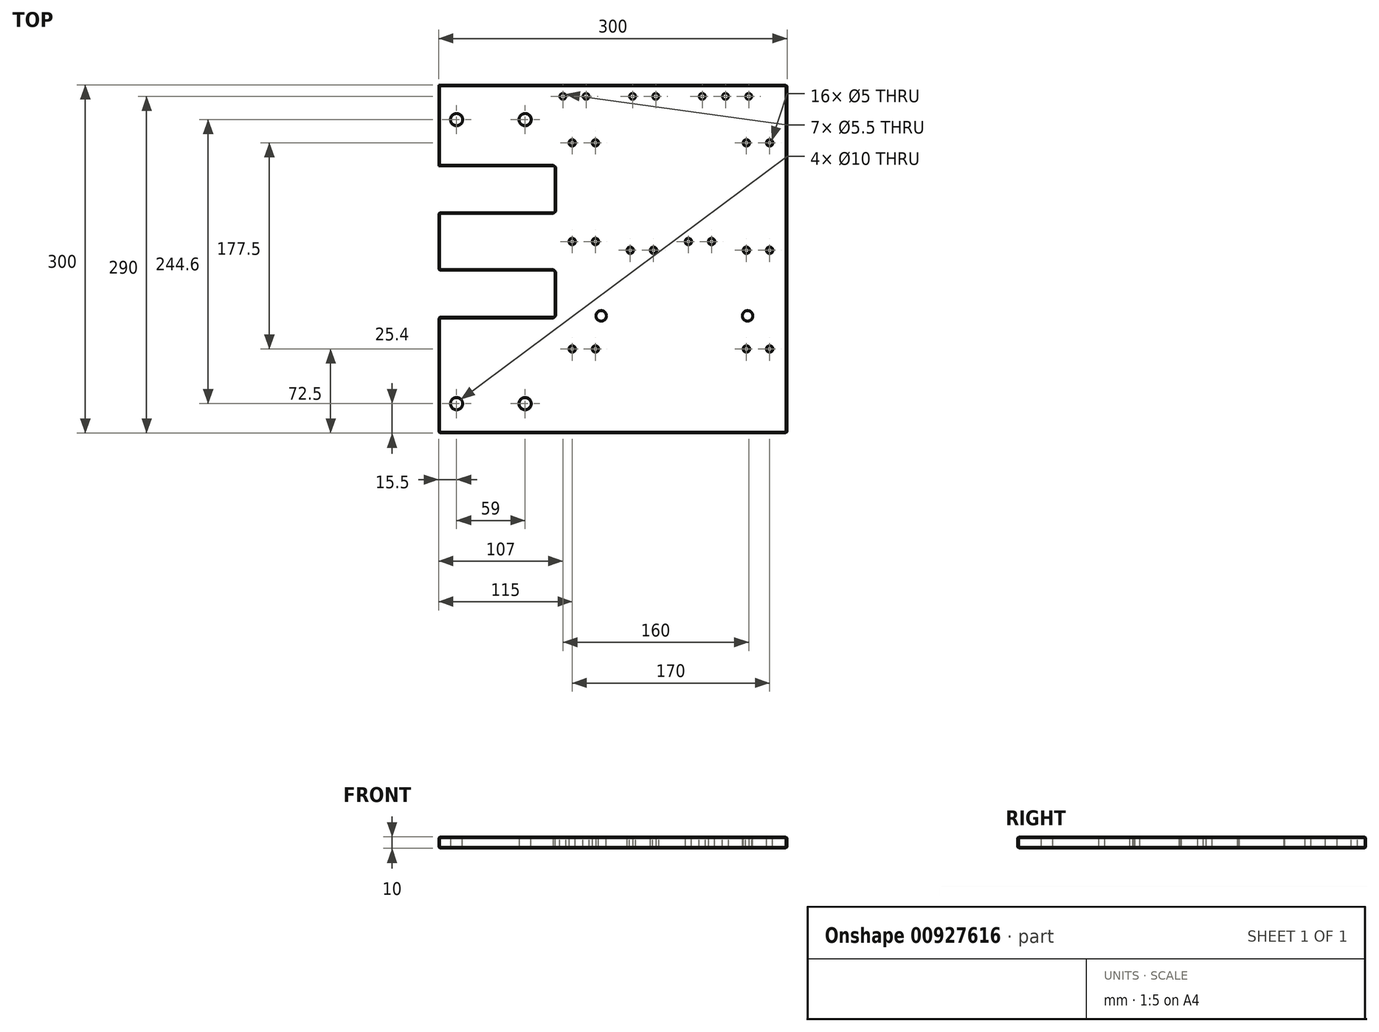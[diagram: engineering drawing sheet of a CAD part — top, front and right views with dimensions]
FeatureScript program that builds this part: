
annotation { "Feature Type Name" : "Feature", "Feature Type Description" : "" }
export const myFeature = defineFeature(function(context is Context, id is Id, definition is map)
    precondition{}
    {
        {
            var Q0;
            Q0=qCreatedBy(makeId("Right.planeOp"),FACE);
            var sketch = newSketch(context, id + "F0", { "sketchPlane" : qUnion([Q0])});
            skLineSegment(sketch, "E0.bottom", {"start": v(-300, 10) * mm, "end": v(0, 10) * mm});
            skLineSegment(sketch, "E0.top", {"start": v(-300, 0) * mm, "end": v(0, 0) * mm});
            skLineSegment(sketch, "E0.left", {"start": v(-300, 10) * mm, "end": v(-300, 0) * mm});
            skLineSegment(sketch, "E0.right", {"start": v(0, 10) * mm, "end": v(0, 0) * mm});
            skSolve(sketch);
        }
        {
            var Q0;
            Q0=makeQuery(id+"F0.imprint","IMPRINT",FACE,{"disambiguationData":[TD([[makeQuery(id+"F0.imprint","IMPRINT",EDGE,{"derivedFrom":sQuery(id+"F0.wireOp",EDGE,"E0.bottom")}),-1.0]])]});
            extrude(context, id + "F1", {"entities" : qUnion([Q0]), "oppositeDirection" : true, "depth" : 300 * mm, "offsetDistance" : 25 * mm});
        }
        {
            var Q0;
            Q0=makeQuery(id+"F1.opExtrude","SWEPT_FACE",FACE,{"disambiguationData":[OSD([sQuery(id+"F0.wireOp",EDGE,"E0.bottom")])]});
            var sketch = newSketch(context, id + "F2", { "sketchPlane" : qUnion([Q0])});
            skLineSegment(sketch, "E1", {"start": v(-329.37, -90) * mm, "end": v(39.16, -90) * mm, "construction": true});
            skLineSegment(sketch, "E2", {"start": v(-320.97, -180) * mm, "end": v(38.29, -180) * mm, "construction": true});
            skLineSegment(sketch, "E3", {"start": v(-327.61, -150) * mm, "end": v(37.4, -150) * mm, "construction": true});
            skLineSegment(sketch, "E4", {"start": v(-300, -70) * mm, "end": v(-200, -70) * mm});
            skLineSegment(sketch, "E5", {"start": v(-200, -70) * mm, "end": v(-200, -90) * mm});
            skLineSegment(sketch, "E6.MirrorCS", {"start": v(-300, -110) * mm, "end": v(-200, -110) * mm});
            skLineSegment(sketch, "E7.MirrorCS", {"start": v(-200, -110) * mm, "end": v(-200, -90) * mm});
            skLineSegment(sketch, "E8", {"start": v(-300, -160) * mm, "end": v(-200, -160) * mm});
            skLineSegment(sketch, "E9", {"start": v(-200, -160) * mm, "end": v(-200, -180) * mm});
            skLineSegment(sketch, "E10.MirrorCS", {"start": v(-300, -200) * mm, "end": v(-200, -200) * mm});
            skLineSegment(sketch, "E11.MirrorCS", {"start": v(-200, -200) * mm, "end": v(-200, -180) * mm});
            skSolve(sketch);
        }
        {
            var Q0;
            Q0=makeQuery(id+"F2.imprint","IMPRINT",FACE,{"disambiguationData":[TD([[makeQuery(id+"F2.imprint","IMPRINT",EDGE,{"derivedFrom":sQuery(id+"F2.wireOp",EDGE,"E5")}),-1.0]])]});
            var Q1;
            {var subQ1=sQuery(id+"F2.wireOp",EDGE,"E8");Q1=makeQuery(id+"F2.imprint","IMPRINT",FACE,{"disambiguationData":[TD([[makeQuery(id+"F2.imprint","IMPRINT",EDGE,{"derivedFrom":subQ1}),-1.0]])]});}
            extrude(context, id + "F3", {"entities" : qUnion([Q0, Q1]), "operationType" : NewBodyOperationType.REMOVE, "endBound" : BoundingType.THROUGH_ALL, "oppositeDirection" : true, "depth" : 25 * mm, "offsetDistance" : 25 * mm});
        }
        {
            var Q0;
            Q0=makeQuery(id+"F1.opExtrude","SWEPT_FACE",FACE,{"disambiguationData":[OSD([sQuery(id+"F0.wireOp",EDGE,"E0.bottom")])]});
            var Q1;
            Q1=makeQuery(id+"F1.opExtrude","SWEPT_FACE",FACE,{"disambiguationData":[OSD([sQuery(id+"F0.wireOp",EDGE,"E0.top")])]});
            var Q2;
            Q2=makeQuery(id+"F1.opExtrude","CAP_EDGE",EDGE,{"disambiguationData":[OSD([sQuery(id+"F0.wireOp",EDGE,"E0.left")])],"isStart":true});
            var Q3;
            Q3=makeQuery(id+"F1.opExtrude","CAP_EDGE",EDGE,{"disambiguationData":[OSD([sQuery(id+"F0.wireOp",EDGE,"E0.right")])],"isStart":true});
            var Q4;
            Q4=makeQuery(id+"FvbSxJF03EfieJc_1.boolean.opBoolean","COPY",EDGE,{"derivedFrom":makeQuery(id+"FvbSxJF03EfieJc_1.opExtrude","SWEPT_EDGE",EDGE,{"disambiguationData":[OSD([sQuery(id+"F0.wireOp",EDGE,"E0.bottom"),sQuery(id+"F0.wireOp",EDGE,"E0.right"),sQuery(id+"FKX7Y40f10C06gv_1.wireOp",EDGE,"pD4dHy5l-zS1k-HRtf-R4PJ-qdT75peHXFwZ")])]})});
            var Q5;
            Q5=makeQuery(id+"FvbSxJF03EfieJc_1.boolean.opBoolean","COPY",EDGE,{"derivedFrom":makeQuery(id+"FvbSxJF03EfieJc_1.opExtrude","SWEPT_EDGE",EDGE,{"disambiguationData":[OSD([sQuery(id+"FKX7Y40f10C06gv_1.wireOp",EDGE,"62FB8XDT-1eOc-TIsZ-BsXp-3CsSRIO25qVi"),sQuery(id+"FKX7Y40f10C06gv_1.wireOp",EDGE,"pD4dHy5l-zS1k-HRtf-R4PJ-qdT75peHXFwZ")])]})});
            var Q6;
            Q6=makeQuery(id+"FvbSxJF03EfieJc_1.boolean.opBoolean","COPY",EDGE,{"derivedFrom":makeQuery(id+"FvbSxJF03EfieJc_1.opExtrude","SWEPT_EDGE",EDGE,{"disambiguationData":[OSD([sQuery(id+"F0.wireOp",EDGE,"E0.bottom"),sQuery(id+"FKX7Y40f10C06gv_1.wireOp",EDGE,"62FB8XDT-1eOc-TIsZ-BsXp-3CsSRIO25qVi")])]})});
            var Q7;
            Q7=makeQuery(id+"F3.boolean.opBoolean","COPY",EDGE,{"derivedFrom":makeQuery(id+"F3.opExtrude","SWEPT_EDGE",EDGE,{"disambiguationData":[OSD([sQuery(id+"F0.wireOp",EDGE,"E0.bottom"),sQuery(id+"F2.wireOp",EDGE,"E4")])]})});
            var Q8;
            Q8=makeQuery(id+"F3.boolean.opBoolean","COPY",FACE,{"derivedFrom":makeQuery(id+"F3.opExtrude","SWEPT_FACE",FACE,{"disambiguationData":[OSD([sQuery(id+"F2.wireOp",EDGE,"E5"),sQuery(id+"F2.wireOp",EDGE,"E7.MirrorCS")])]})});
            var Q9;
            {var subQ0=sQuery(id+"F0.wireOp",EDGE,"E0.bottom");var subQ1=sQuery(id+"F0.wireOp",EDGE,"E0.top");Q9=makeQuery(id+"F3.boolean.opBoolean","SPLIT",FACE,{"disambiguationData":[TD([makeQuery(id+"F3.opExtrude","SWEPT_FACE",FACE,{"disambiguationData":[OSD([sQuery(id+"F2.wireOp",EDGE,"E6.MirrorCS")])]})])],"derivedFrom":makeQuery(id+"F1.opExtrude","CAP_FACE",FACE,{"disambiguationData":[OSD([subQ0,subQ1,sQuery(id+"F0.wireOp",EDGE,"E0.left"),sQuery(id+"F0.wireOp",EDGE,"E0.right")])],"isStart":false})});}
            var Q10;
            Q10=makeQuery(id+"F3.boolean.opBoolean","COPY",FACE,{"derivedFrom":makeQuery(id+"F3.opExtrude","SWEPT_FACE",FACE,{"disambiguationData":[OSD([sQuery(id+"F2.wireOp",EDGE,"E9"),sQuery(id+"F2.wireOp",EDGE,"E11.MirrorCS")])]})});
            var Q11;
            {var subQ0=sQuery(id+"F0.wireOp",EDGE,"E0.bottom");var subQ1=sQuery(id+"F0.wireOp",EDGE,"E0.top");var subQ2=sQuery(id+"F0.wireOp",EDGE,"E0.left");Q11=makeQuery(id+"F3.boolean.opBoolean","SPLIT",FACE,{"disambiguationData":[TD([makeQuery(id+"F1.opExtrude","SWEPT_FACE",FACE,{"disambiguationData":[OSD([subQ2])]})])],"derivedFrom":makeQuery(id+"F1.opExtrude","CAP_FACE",FACE,{"disambiguationData":[OSD([subQ0,subQ1,subQ2,sQuery(id+"F0.wireOp",EDGE,"E0.right")])],"isStart":false})});}
            var Q12;
            Q12=makeQuery(id+"FvbSxJF03EfieJc_1.boolean.opBoolean","COPY",FACE,{"derivedFrom":makeQuery(id+"FvbSxJF03EfieJc_1.opExtrude","SWEPT_FACE",FACE,{"disambiguationData":[OSD([sQuery(id+"FKX7Y40f10C06gv_1.wireOp",EDGE,"HtusyhB6-mlgM-k3YL-Usch-LdjpPYYtbepC")])]})});
            chamfer(context, id + "F4", {"entities" : qUnion([Q0, Q1, Q2, Q3, Q4, Q5, Q6, Q7, Q8, Q9, Q10, Q11, Q12]), "width" : 1 * mm, "tangentPropagation" : true});
        }
        {
            var Q0;
            Q0=makeQuery(id+"F1.opExtrude","SWEPT_FACE",FACE,{"disambiguationData":[OSD([sQuery(id+"F0.wireOp",EDGE,"E0.bottom")])]});
            var sketch = newSketch(context, id + "F5", { "sketchPlane" : qUnion([Q0])});
            skLineSegment(sketch, "E12", {"start": v(-257.2, -50) * mm, "end": v(69.47, -50) * mm, "construction": true});
            skCircle(sketch, "E13", {"center": v(-15, -50) * mm, "radius": 2.5 * mm});
            skCircle(sketch, "E14", {"center": v(-35, -50) * mm, "radius": 2.5 * mm});
            skCircle(sketch, "E15", {"center": v(-165, -50) * mm, "radius": 2.5 * mm});
            skCircle(sketch, "E16", {"center": v(-185, -50) * mm, "radius": 2.5 * mm});
            skLineSegment(sketch, "E17", {"start": v(-259.68, -92.5) * mm, "end": v(66.53, -92.5) * mm, "construction": true});
            skCircle(sketch, "E18.MirrorC", {"center": v(-65, -135) * mm, "radius": 2.5 * mm});
            skCircle(sketch, "E19.MirrorC", {"center": v(-85, -135) * mm, "radius": 2.5 * mm});
            skCircle(sketch, "E20.MirrorC", {"center": v(-165, -135) * mm, "radius": 2.5 * mm});
            skCircle(sketch, "E21.MirrorC", {"center": v(-185, -135) * mm, "radius": 2.5 * mm});
            skLineSegment(sketch, "E22", {"start": v(-226.56, -135) * mm, "end": v(93.62, -135) * mm, "construction": true});
            skLineSegment(sketch, "E23", {"start": v(-248.87, -227.5) * mm, "end": v(106.4, -227.5) * mm, "construction": true});
            skCircle(sketch, "E24", {"center": v(-15, -227.5) * mm, "radius": 2.5 * mm});
            skCircle(sketch, "E25", {"center": v(-35, -227.5) * mm, "radius": 2.5 * mm});
            skCircle(sketch, "E26", {"center": v(-165, -227.5) * mm, "radius": 2.5 * mm});
            skCircle(sketch, "E27", {"center": v(-185, -227.5) * mm, "radius": 2.5 * mm});
            skLineSegment(sketch, "E28", {"start": v(-223.77, -185) * mm, "end": v(39.9, -185) * mm, "construction": true});
            skCircle(sketch, "E29.MirrorC", {"center": v(-15, -142.5) * mm, "radius": 2.5 * mm});
            skCircle(sketch, "E30.MirrorC", {"center": v(-35, -142.5) * mm, "radius": 2.5 * mm});
            skCircle(sketch, "E31.MirrorC", {"center": v(-115, -142.5) * mm, "radius": 2.5 * mm});
            skCircle(sketch, "E32.MirrorC", {"center": v(-135, -142.5) * mm, "radius": 2.5 * mm});
            skLineSegment(sketch, "E33", {"start": v(-216.85, -142.5) * mm, "end": v(47.22, -142.5) * mm, "construction": true});
            skSolve(sketch);
        }
        {
            var Q0;
            Q0 = qSketchRegion(id + "F5", true);
            extrude(context, id + "F6", {"entities" : qUnion([Q0]), "operationType" : NewBodyOperationType.REMOVE, "oppositeDirection" : true, "depth" : 25 * mm, "offsetDistance" : 25 * mm});
        }
        {
            var Q0;
            Q0=makeQuery(id+"F6.boolean.opBoolean","COPY",FACE,{"derivedFrom":makeQuery(id+"F6.opExtrude","SWEPT_FACE",FACE,{"disambiguationData":[OSD([sQuery(id+"F5.wireOp",EDGE,"E13")])]})});
            var Q1;
            Q1=makeQuery(id+"F6.boolean.opBoolean","COPY",FACE,{"derivedFrom":makeQuery(id+"F6.opExtrude","SWEPT_FACE",FACE,{"disambiguationData":[OSD([sQuery(id+"F5.wireOp",EDGE,"E14")])]})});
            var Q2;
            Q2=makeQuery(id+"F6.boolean.opBoolean","COPY",FACE,{"derivedFrom":makeQuery(id+"F6.opExtrude","SWEPT_FACE",FACE,{"disambiguationData":[OSD([sQuery(id+"F5.wireOp",EDGE,"gajHNEhn-UsBA-cIE7-0buz-QHXoqe9fZdcb")])]})});
            var Q3;
            Q3=makeQuery(id+"F6.boolean.opBoolean","COPY",FACE,{"derivedFrom":makeQuery(id+"F6.opExtrude","SWEPT_FACE",FACE,{"disambiguationData":[OSD([sQuery(id+"F5.wireOp",EDGE,"lTrSfhLt-ZZyG-1LEB-Uh49-cvV0hC45FU28")])]})});
            var Q4;
            Q4=makeQuery(id+"F6.boolean.opBoolean","COPY",FACE,{"derivedFrom":makeQuery(id+"F6.opExtrude","SWEPT_FACE",FACE,{"disambiguationData":[OSD([sQuery(id+"F5.wireOp",EDGE,"RGiTn3fd-h3rd-NjaM-kyKq-MnqPz9M8kedh")])]})});
            var Q5;
            Q5=makeQuery(id+"F6.boolean.opBoolean","COPY",FACE,{"derivedFrom":makeQuery(id+"F6.opExtrude","SWEPT_FACE",FACE,{"disambiguationData":[OSD([sQuery(id+"F5.wireOp",EDGE,"BAnZuRCm-gk1o-uBdQ-ohAz-i2KR7L9J03BO")])]})});
            var Q6;
            Q6=makeQuery(id+"F6.boolean.opBoolean","COPY",FACE,{"derivedFrom":makeQuery(id+"F6.opExtrude","SWEPT_FACE",FACE,{"disambiguationData":[OSD([sQuery(id+"F5.wireOp",EDGE,"E15")])]})});
            var Q7;
            Q7=makeQuery(id+"F6.boolean.opBoolean","COPY",FACE,{"derivedFrom":makeQuery(id+"F6.opExtrude","SWEPT_FACE",FACE,{"disambiguationData":[OSD([sQuery(id+"F5.wireOp",EDGE,"E16")])]})});
            var Q8;
            Q8=makeQuery(id+"F6.boolean.opBoolean","COPY",FACE,{"derivedFrom":makeQuery(id+"F6.opExtrude","SWEPT_FACE",FACE,{"disambiguationData":[OSD([sQuery(id+"F5.wireOp",EDGE,"1afade6a-c68f-400e-9332-eec06feb96f50.MirrorC")])]})});
            var Q9;
            Q9=makeQuery(id+"F6.boolean.opBoolean","COPY",FACE,{"derivedFrom":makeQuery(id+"F6.opExtrude","SWEPT_FACE",FACE,{"disambiguationData":[OSD([sQuery(id+"F5.wireOp",EDGE,"a24478ff-3b3c-47b1-bfc6-6543900dc0290.MirrorC")])]})});
            var Q10;
            Q10=makeQuery(id+"F6.boolean.opBoolean","COPY",FACE,{"derivedFrom":makeQuery(id+"F6.opExtrude","SWEPT_FACE",FACE,{"disambiguationData":[OSD([sQuery(id+"F5.wireOp",EDGE,"E18.MirrorC")])]})});
            var Q11;
            Q11=makeQuery(id+"F6.boolean.opBoolean","COPY",FACE,{"derivedFrom":makeQuery(id+"F6.opExtrude","SWEPT_FACE",FACE,{"disambiguationData":[OSD([sQuery(id+"F5.wireOp",EDGE,"E19.MirrorC")])]})});
            var Q12;
            Q12=makeQuery(id+"F6.boolean.opBoolean","COPY",FACE,{"derivedFrom":makeQuery(id+"F6.opExtrude","SWEPT_FACE",FACE,{"disambiguationData":[OSD([sQuery(id+"F5.wireOp",EDGE,"ee7517f6-939b-4303-b834-303614dda3ea0.MirrorC")])]})});
            var Q13;
            Q13=makeQuery(id+"F6.boolean.opBoolean","COPY",FACE,{"derivedFrom":makeQuery(id+"F6.opExtrude","SWEPT_FACE",FACE,{"disambiguationData":[OSD([sQuery(id+"F5.wireOp",EDGE,"fb28a4bd-bbee-47cf-9a3b-2ebf1eba7eac0.MirrorC")])]})});
            var Q14;
            Q14=makeQuery(id+"F6.boolean.opBoolean","COPY",FACE,{"derivedFrom":makeQuery(id+"F6.opExtrude","SWEPT_FACE",FACE,{"disambiguationData":[OSD([sQuery(id+"F5.wireOp",EDGE,"E21.MirrorC")])]})});
            var Q15;
            Q15=makeQuery(id+"F6.boolean.opBoolean","COPY",FACE,{"derivedFrom":makeQuery(id+"F6.opExtrude","SWEPT_FACE",FACE,{"disambiguationData":[OSD([sQuery(id+"F5.wireOp",EDGE,"E20.MirrorC")])]})});
            var Q16;
            Q16=makeQuery(id+"F6.boolean.opBoolean","COPY",FACE,{"derivedFrom":makeQuery(id+"F6.opExtrude","SWEPT_FACE",FACE,{"disambiguationData":[OSD([sQuery(id+"F5.wireOp",EDGE,"E29.MirrorC")])]})});
            var Q17;
            Q17=makeQuery(id+"F6.boolean.opBoolean","COPY",FACE,{"derivedFrom":makeQuery(id+"F6.opExtrude","SWEPT_FACE",FACE,{"disambiguationData":[OSD([sQuery(id+"F5.wireOp",EDGE,"E30.MirrorC")])]})});
            var Q18;
            Q18=makeQuery(id+"F6.boolean.opBoolean","COPY",FACE,{"derivedFrom":makeQuery(id+"F6.opExtrude","SWEPT_FACE",FACE,{"disambiguationData":[OSD([sQuery(id+"F5.wireOp",EDGE,"E31.MirrorC")])]})});
            var Q19;
            Q19=makeQuery(id+"F6.boolean.opBoolean","COPY",FACE,{"derivedFrom":makeQuery(id+"F6.opExtrude","SWEPT_FACE",FACE,{"disambiguationData":[OSD([sQuery(id+"F5.wireOp",EDGE,"E32.MirrorC")])]})});
            var Q20;
            Q20=makeQuery(id+"F6.boolean.opBoolean","COPY",FACE,{"derivedFrom":makeQuery(id+"F6.opExtrude","SWEPT_FACE",FACE,{"disambiguationData":[OSD([sQuery(id+"F5.wireOp",EDGE,"E24")])]})});
            var Q21;
            Q21=makeQuery(id+"F6.boolean.opBoolean","COPY",FACE,{"derivedFrom":makeQuery(id+"F6.opExtrude","SWEPT_FACE",FACE,{"disambiguationData":[OSD([sQuery(id+"F5.wireOp",EDGE,"E25")])]})});
            var Q22;
            Q22=makeQuery(id+"F6.boolean.opBoolean","COPY",FACE,{"derivedFrom":makeQuery(id+"F6.opExtrude","SWEPT_FACE",FACE,{"disambiguationData":[OSD([sQuery(id+"F5.wireOp",EDGE,"E26")])]})});
            var Q23;
            Q23=makeQuery(id+"F6.boolean.opBoolean","COPY",FACE,{"derivedFrom":makeQuery(id+"F6.opExtrude","SWEPT_FACE",FACE,{"disambiguationData":[OSD([sQuery(id+"F5.wireOp",EDGE,"E27")])]})});
            chamfer(context, id + "F7", {"entities" : qUnion([Q0, Q1, Q2, Q3, Q4, Q5, Q6, Q7, Q8, Q9, Q10, Q11, Q12, Q13, Q14, Q15, Q16, Q17, Q18, Q19, Q20, Q21, Q22, Q23]), "width" : 0.5 * mm, "tangentPropagation" : true});
        }
        {
            var Q0;
            Q0=makeQuery(id+"F1.opExtrude","SWEPT_FACE",FACE,{"disambiguationData":[OSD([sQuery(id+"F0.wireOp",EDGE,"E0.bottom")])]});
            var sketch = newSketch(context, id + "F8", { "sketchPlane" : qUnion([Q0])});
            skLineSegment(sketch, "E34", {"start": v(-337.77, -274.6) * mm, "end": v(66.9, -274.6) * mm, "construction": true});
            skLineSegment(sketch, "E35", {"start": v(-284.5, -215.9) * mm, "end": v(-284.5, -343.43) * mm, "construction": true});
            skCircle(sketch, "E36", {"center": v(-284.5, -274.6) * mm, "radius": 5 * mm});
            skCircle(sketch, "E37.1.0.0", {"center": v(-225.5, -274.6) * mm, "radius": 5 * mm});
            skLineSegment(sketch, "E37.direction1", {"start": v(-284.5, -274.6) * mm, "end": v(-225.5, -274.6) * mm, "construction": true});
            skLineSegment(sketch, "E38", {"start": v(-329.7, -30) * mm, "end": v(25.4, -30) * mm, "construction": true});
            skLineSegment(sketch, "E39", {"start": v(-284.5, 17.2) * mm, "end": v(-284.5, -84.8) * mm, "construction": true});
            skCircle(sketch, "E40", {"center": v(-284.5, -30) * mm, "radius": 5 * mm});
            skCircle(sketch, "E41.1.0.0", {"center": v(-225.5, -30) * mm, "radius": 5 * mm});
            skLineSegment(sketch, "E41.direction1", {"start": v(-284.5, -30) * mm, "end": v(-225.5, -30) * mm, "construction": true});
            skLineSegment(sketch, "E42", {"start": v(-255, 49.02) * mm, "end": v(-255, -396.2) * mm, "construction": true});
            skSolve(sketch);
        }
        {
            var Q0;
            Q0 = qSketchRegion(id + "F8", true);
            extrude(context, id + "F9", {"entities" : qUnion([Q0]), "operationType" : NewBodyOperationType.REMOVE, "endBound" : BoundingType.THROUGH_ALL, "oppositeDirection" : true, "depth" : 25 * mm, "offsetDistance" : 25 * mm});
        }
        {
            var Q0;
            Q0=makeQuery(id+"F9.boolean.opBoolean","COPY",FACE,{"derivedFrom":makeQuery(id+"F9.opExtrude","SWEPT_FACE",FACE,{"disambiguationData":[OSD([sQuery(id+"F8.wireOp",EDGE,"E40")])]})});
            var Q1;
            Q1=makeQuery(id+"F9.boolean.opBoolean","COPY",FACE,{"derivedFrom":makeQuery(id+"F9.opExtrude","SWEPT_FACE",FACE,{"disambiguationData":[OSD([sQuery(id+"F8.wireOp",EDGE,"E41.1.0.0")])]})});
            var Q2;
            Q2=makeQuery(id+"F9.boolean.opBoolean","COPY",FACE,{"derivedFrom":makeQuery(id+"F9.opExtrude","SWEPT_FACE",FACE,{"disambiguationData":[OSD([sQuery(id+"F8.wireOp",EDGE,"E36")])]})});
            var Q3;
            Q3=makeQuery(id+"F9.boolean.opBoolean","COPY",FACE,{"derivedFrom":makeQuery(id+"F9.opExtrude","SWEPT_FACE",FACE,{"disambiguationData":[OSD([sQuery(id+"F8.wireOp",EDGE,"E37.1.0.0")])]})});
            chamfer(context, id + "F10", {"entities" : qUnion([Q0, Q1, Q2, Q3]), "width" : 0.5 * mm, "tangentPropagation" : true});
        }
        {
            var Q0;
            Q0=makeQuery(id+"F1.opExtrude","SWEPT_FACE",FACE,{"disambiguationData":[OSD([sQuery(id+"F0.wireOp",EDGE,"E0.bottom")])]});
            var sketch = newSketch(context, id + "F11", { "sketchPlane" : qUnion([Q0])});
            skLineSegment(sketch, "E43", {"start": v(-279.44, -205) * mm, "end": v(30.36, -205) * mm, "construction": true});
            skLineSegment(sketch, "E44", {"start": v(-20, -111.64) * mm, "end": v(-20, -310.67) * mm, "construction": true});
            skPoint(sketch, "E45", {"position": v(-20, -205) * mm});
            skLineSegment(sketch, "E46.bottom", {"start": v(-20, -205) * mm, "end": v(-174, -205) * mm});
            skLineSegment(sketch, "E46.top", {"start": v(-20, -193) * mm, "end": v(-174, -193) * mm});
            skLineSegment(sketch, "E46.left", {"start": v(-20, -205) * mm, "end": v(-20, -193) * mm});
            skLineSegment(sketch, "E46.right", {"start": v(-174, -205) * mm, "end": v(-174, -193) * mm});
            skLineSegment(sketch, "E47", {"start": v(-182, -199) * mm, "end": v(-13.34, -199) * mm, "construction": true});
            skPoint(sketch, "E47.startSnap0", {"position": v(-174, -199) * mm});
            skPoint(sketch, "E47.endSnap0", {"position": v(-20, -199) * mm});
            skCircle(sketch, "E48", {"center": v(-160, -199) * mm, "radius": 4.25 * mm});
            skCircle(sketch, "E49", {"center": v(-34, -199) * mm, "radius": 4.25 * mm});
            skLineSegment(sketch, "E50", {"start": v(-94, -151.24) * mm, "end": v(-94, -260.65) * mm, "construction": true});
            skLineSegment(sketch, "E51", {"start": v(-255, -124.71) * mm, "end": v(-255, -341.62) * mm, "construction": true});
            skSolve(sketch);
        }
        {
            var Q0;
            Q0=makeQuery(id+"F11.imprint","IMPRINT",FACE,{"disambiguationData":[TD([[makeQuery(id+"F11.imprint","IMPRINT",EDGE,{"derivedFrom":sQuery(id+"F11.wireOp",EDGE,"E49")}),1.0]])]});
            var Q1;
            Q1=makeQuery(id+"F11.imprint","IMPRINT",FACE,{"disambiguationData":[TD([[makeQuery(id+"F11.imprint","IMPRINT",EDGE,{"derivedFrom":sQuery(id+"F11.wireOp",EDGE,"E48")}),1.0]])]});
            extrude(context, id + "F12", {"entities" : qUnion([Q0, Q1]), "operationType" : NewBodyOperationType.REMOVE, "endBound" : BoundingType.THROUGH_ALL, "oppositeDirection" : true, "depth" : 25 * mm, "offsetDistance" : 25 * mm});
        }
        {
            var Q0;
            Q0=makeQuery(id+"F12.boolean.opBoolean","COPY",FACE,{"derivedFrom":makeQuery(id+"F12.opExtrude","SWEPT_FACE",FACE,{"disambiguationData":[OSD([sQuery(id+"F11.wireOp",EDGE,"E48")])]})});
            var Q1;
            Q1=makeQuery(id+"F12.boolean.opBoolean","COPY",FACE,{"derivedFrom":makeQuery(id+"F12.opExtrude","SWEPT_FACE",FACE,{"disambiguationData":[OSD([sQuery(id+"F11.wireOp",EDGE,"E49")])]})});
            chamfer(context, id + "F13", {"entities" : qUnion([Q0, Q1]), "width" : 0.5 * mm, "tangentPropagation" : true});
        }
        {
            var Q0;
            Q0=makeQuery(id+"F1.opExtrude","SWEPT_FACE",FACE,{"disambiguationData":[OSD([sQuery(id+"F0.wireOp",EDGE,"E0.bottom")])]});
            var sketch = newSketch(context, id + "F14", { "sketchPlane" : qUnion([Q0])});
            skLineSegment(sketch, "E52", {"start": v(-334.74, -10) * mm, "end": v(74.03, -10) * mm, "construction": true});
            skLineSegment(sketch, "E53", {"start": v(-193, 49.45) * mm, "end": v(-193, -102.26) * mm, "construction": true});
            skLineSegment(sketch, "E54.0", {"start": v(-173, 49.45) * mm, "end": v(-173, -102.26) * mm, "construction": true});
            skLineSegment(sketch, "E55", {"start": v(-133, 24.18) * mm, "end": v(-133, -47.45) * mm, "construction": true});
            skLineSegment(sketch, "E56", {"start": v(-113, 23.25) * mm, "end": v(-113, -47.92) * mm, "construction": true});
            skLineSegment(sketch, "E57", {"start": v(-73, 25.42) * mm, "end": v(-73, -50.55) * mm, "construction": true});
            skLineSegment(sketch, "E58", {"start": v(-53, 24.96) * mm, "end": v(-53, -50.24) * mm, "construction": true});
            skCircle(sketch, "E59", {"center": v(-193, -10) * mm, "radius": 2.75 * mm});
            skCircle(sketch, "E60", {"center": v(-173, -10) * mm, "radius": 2.75 * mm});
            skCircle(sketch, "E61", {"center": v(-133, -10) * mm, "radius": 2.75 * mm});
            skCircle(sketch, "E62", {"center": v(-113, -10) * mm, "radius": 2.75 * mm});
            skCircle(sketch, "E63", {"center": v(-73, -10) * mm, "radius": 2.75 * mm});
            skCircle(sketch, "E64", {"center": v(-53, -10) * mm, "radius": 2.75 * mm});
            skLineSegment(sketch, "E65", {"start": v(-33, 25.2) * mm, "end": v(-33, -43.7) * mm, "construction": true});
            skCircle(sketch, "E66", {"center": v(-33, -10) * mm, "radius": 2.75 * mm});
            skSolve(sketch);
        }
        {
            var Q0;
            Q0 = qSketchRegion(id + "F14", true);
            extrude(context, id + "F15", {"entities" : qUnion([Q0]), "operationType" : NewBodyOperationType.REMOVE, "endBound" : BoundingType.THROUGH_ALL, "oppositeDirection" : true, "depth" : 25 * mm, "offsetDistance" : 25 * mm});
        }
    });
